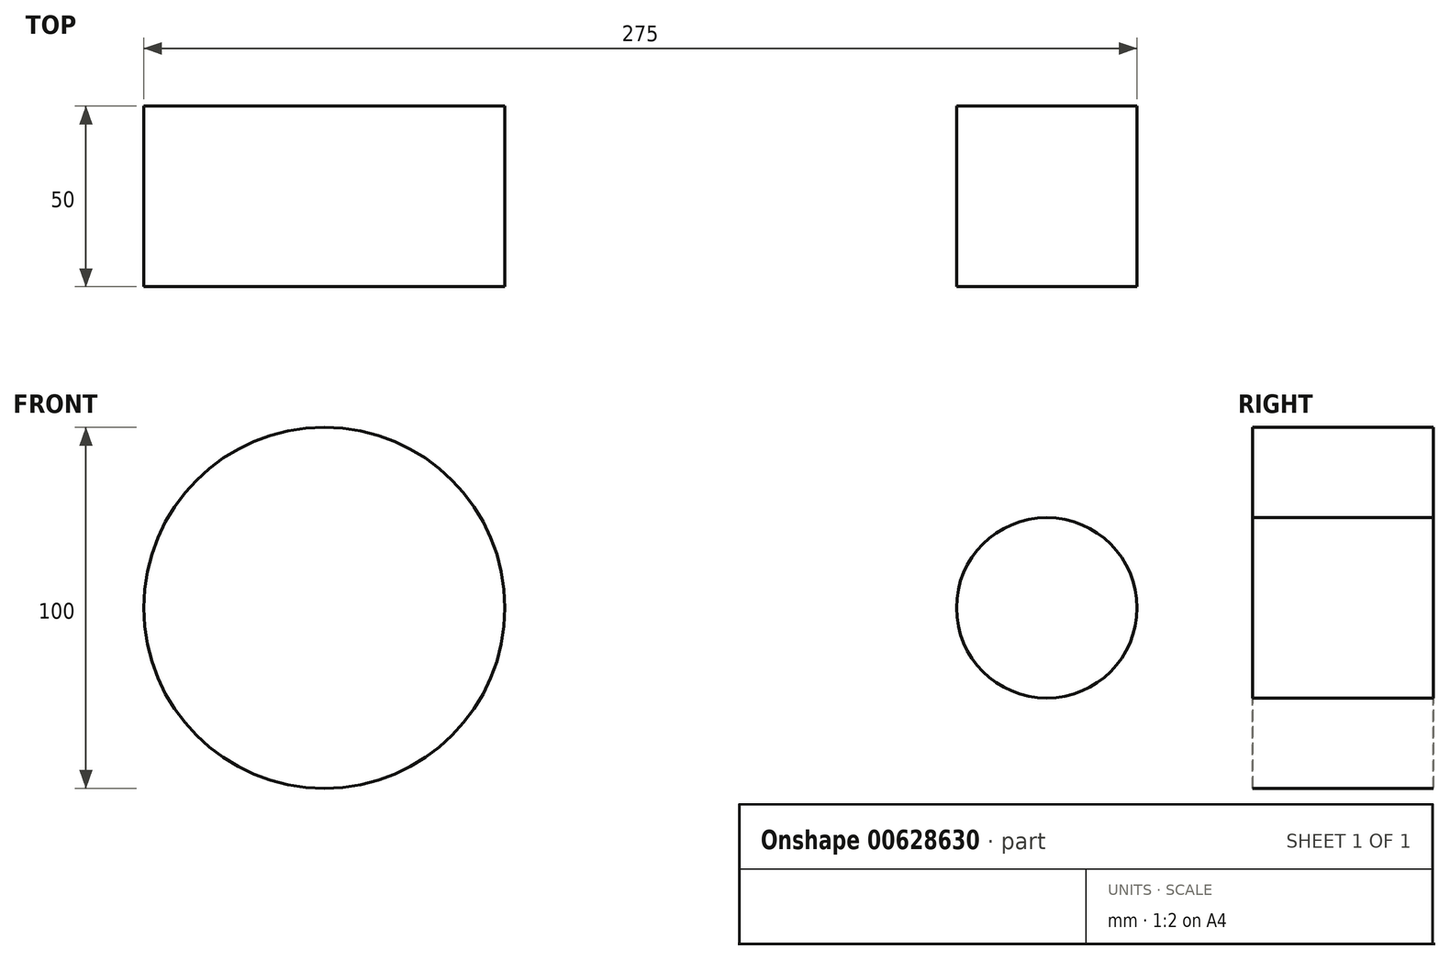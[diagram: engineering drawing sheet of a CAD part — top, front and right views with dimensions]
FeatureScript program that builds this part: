
annotation { "Feature Type Name" : "Feature", "Feature Type Description" : "" }
export const myFeature = defineFeature(function(context is Context, id is Id, definition is map)
    precondition{}
    {
        {
            var Q0;
            Q0=qCreatedBy(makeId("Front.planeOp"),FACE);
            var sketch = newSketch(context, id + "F0", { "sketchPlane" : qUnion([Q0])});
            skCircle(sketch, "E0", {"center": v(0, 0) * mm, "radius": 50 * mm});
            skCircle(sketch, "E1", {"center": v(200, 0) * mm, "radius": 25 * mm});
            skSolve(sketch);
        }
        {
            var Q0;
            Q0 = qSketchRegion(id + "F0", true);
            var Q1;
            Q1=makeQuery(id+"F0.imprint","IMPRINT",FACE,{"disambiguationData":[TD([[makeQuery(id+"F0.imprint","IMPRINT",EDGE,{"derivedFrom":sQuery(id+"F0.wireOp",EDGE,"E0")}),1.0]])]});
            extrude(context, id + "F1", {"entities" : qUnion([Q0, Q1]), "depth" : 50 * mm, "offsetDistance" : 25 * mm});
        }
    });
